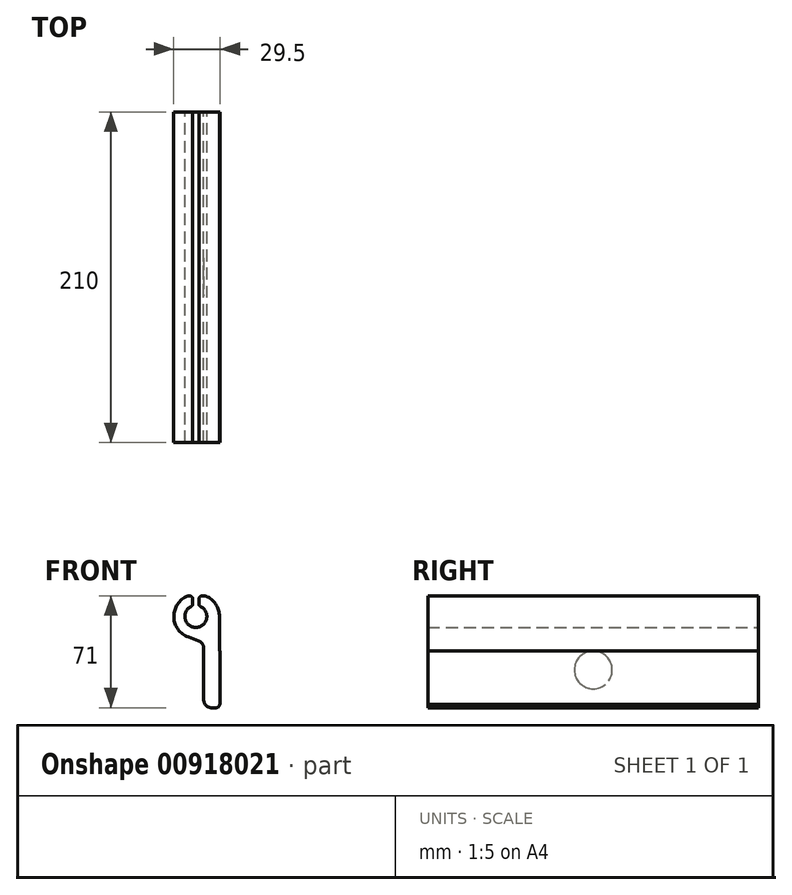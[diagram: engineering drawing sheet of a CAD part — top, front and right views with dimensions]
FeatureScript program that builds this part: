
annotation { "Feature Type Name" : "Feature", "Feature Type Description" : "" }
export const myFeature = defineFeature(function(context is Context, id is Id, definition is map)
    precondition{}
    {
        {
            var Q0;
            Q0=qCreatedBy(makeId("Front.planeOp"),FACE);
            var sketch = newSketch(context, id + "F0", { "sketchPlane" : qUnion([Q0])});
            skArc(sketch, "E0", {"start": v(4.5, -30.5) * mm, "mid": v(5.96, -34.04) * mm, "end": v(9.5, -35.5) * mm});
            skLineSegment(sketch, "E1", {"start": v(9.5, -35.5) * mm, "end": v(12.5, -35.5) * mm});
            skArc(sketch, "E2", {"start": v(12.5, -35.5) * mm, "mid": v(13.91, -34.91) * mm, "end": v(14.5, -33.5) * mm});
            skLineSegment(sketch, "E3", {"start": v(14.5, -33.5) * mm, "end": v(14.5, 22.5) * mm});
            skArc(sketch, "E4", {"start": v(14.5, 22.5) * mm, "mid": v(12.45, 29.79) * mm, "end": v(6.91, 34.94) * mm});
            skArc(sketch, "E5", {"start": v(6.91, 34.94) * mm, "mid": v(5.8, 35.36) * mm, "end": v(4.62, 35.5) * mm});
            skLineSegment(sketch, "E6", {"start": v(4.62, 35.5) * mm, "end": v(3.5, 35.5) * mm});
            skArc(sketch, "E7", {"start": v(3.5, 35.5) * mm, "mid": v(2.09, 34.91) * mm, "end": v(1.5, 33.5) * mm});
            skLineSegment(sketch, "E8", {"start": v(1.5, 33.5) * mm, "end": v(1.5, 30.25) * mm});
            skArc(sketch, "E9", {"start": v(1.5, 30.25) * mm, "mid": v(1.74, 29.43) * mm, "end": v(2.38, 28.88) * mm});
            skArc(sketch, "E10", {"start": v(-3.38, 28.88) * mm, "mid": v(-0.5, 15.5) * mm, "end": v(2.38, 28.88) * mm});
            skArc(sketch, "E11", {"start": v(-3.38, 28.88) * mm, "mid": v(-2.74, 29.43) * mm, "end": v(-2.5, 30.25) * mm});
            skLineSegment(sketch, "E12", {"start": v(-2.5, 30.25) * mm, "end": v(-2.5, 33.5) * mm});
            skArc(sketch, "E13", {"start": v(-2.5, 33.5) * mm, "mid": v(-3.09, 34.91) * mm, "end": v(-4.5, 35.5) * mm});
            skLineSegment(sketch, "E14", {"start": v(-4.5, 35.5) * mm, "end": v(-4.62, 35.5) * mm});
            skArc(sketch, "E15", {"start": v(-4.62, 35.5) * mm, "mid": v(-5.8, 35.36) * mm, "end": v(-6.91, 34.94) * mm});
            skArc(sketch, "E16", {"start": v(-6.91, 34.94) * mm, "mid": v(-14.47, 21.61) * mm, "end": v(-5.29, 9.34) * mm});
            skLineSegment(sketch, "E17", {"start": v(-5.29, 9.34) * mm, "end": v(1.21, 6.98) * mm});
            skArc(sketch, "E18", {"start": v(4.5, 2.28) * mm, "mid": v(3.6, 5.15) * mm, "end": v(1.21, 6.98) * mm});
            skLineSegment(sketch, "E19", {"start": v(4.5, 2.28) * mm, "end": v(4.5, -30.5) * mm});
            skLineSegment(sketch, "E20", {"start": v(4.5, -23.5) * mm, "end": v(4.4, -23.5) * mm});
            skLineSegment(sketch, "E21", {"start": v(4.4, -23.5) * mm, "end": v(4.4, 0.5) * mm});
            skLineSegment(sketch, "E22", {"start": v(4.4, 0.5) * mm, "end": v(4.5, 0.5) * mm});
            skSolve(sketch);
        }
        {
            var Q0;
            {var subQ0=sQuery(id+"F0.wireOp",EDGE,"E0");Q0=makeQuery(id+"F0.imprint","IMPRINT",FACE,{"disambiguationData":[TD([[makeQuery(id+"F0.imprint","IMPRINT",EDGE,{"derivedFrom":subQ0}),1.0]])]});}
            extrude(context, id + "F1", {"entities" : qUnion([Q0]), "endBound" : BoundingType.SYMMETRIC, "depth" : 210 * mm, "offsetDistance" : 25 * mm});
        }
        {
            var Q0;
            Q0=makeQuery(id+"F1.opExtrude","SWEPT_FACE",FACE,{"disambiguationData":[OSD([sQuery(id+"F0.wireOp",EDGE,"E19")])]});
            var sketch = newSketch(context, id + "F2", { "sketchPlane" : qUnion([Q0])});
            skCircle(sketch, "E23", {"center": v(0, -11.5) * mm, "radius": 12 * mm});
            skSolve(sketch);
        }
        {
            var Q0;
            Q0=makeQuery(id+"F2.imprint","IMPRINT",FACE,{"disambiguationData":[TD([[makeQuery(id+"F2.imprint","IMPRINT",EDGE,{"derivedFrom":sQuery(id+"F2.wireOp",EDGE,"E23")}),1.0]])]});
            extrude(context, id + "F3", {"entities" : qUnion([Q0]), "operationType" : NewBodyOperationType.ADD, "depth" : 0.05 * mm, "offsetDistance" : 25 * mm});
        }
        {
            var Q0;
            Q0=makeQuery(id+"F1.opExtrude","SWEPT_FACE",FACE,{"disambiguationData":[OSD([sQuery(id+"F0.wireOp",EDGE,"E3")])]});
            var sketch = newSketch(context, id + "F4", { "sketchPlane" : qUnion([Q0])});
            skLineSegment(sketch, "E24", {"start": v(-105, 0.5) * mm, "end": v(105, 0.5) * mm});
            skSolve(sketch);
        }
        {
            var Q0;
            {var subQ0=sQuery(id+"F4.wireOp",EDGE,"E24");Q0=makeQuery(id+"F4.imprint","IMPRINT",FACE,{"disambiguationData":[TD([[makeQuery(id+"F4.imprint","IMPRINT",EDGE,{"derivedFrom":subQ0}),-1.0]])]});}
            extrude(context, id + "F5", {"entities" : qUnion([Q0]), "operationType" : NewBodyOperationType.ADD, "depth" : .5 * mm, "offsetDistance" : 25 * mm});
        }
    });
